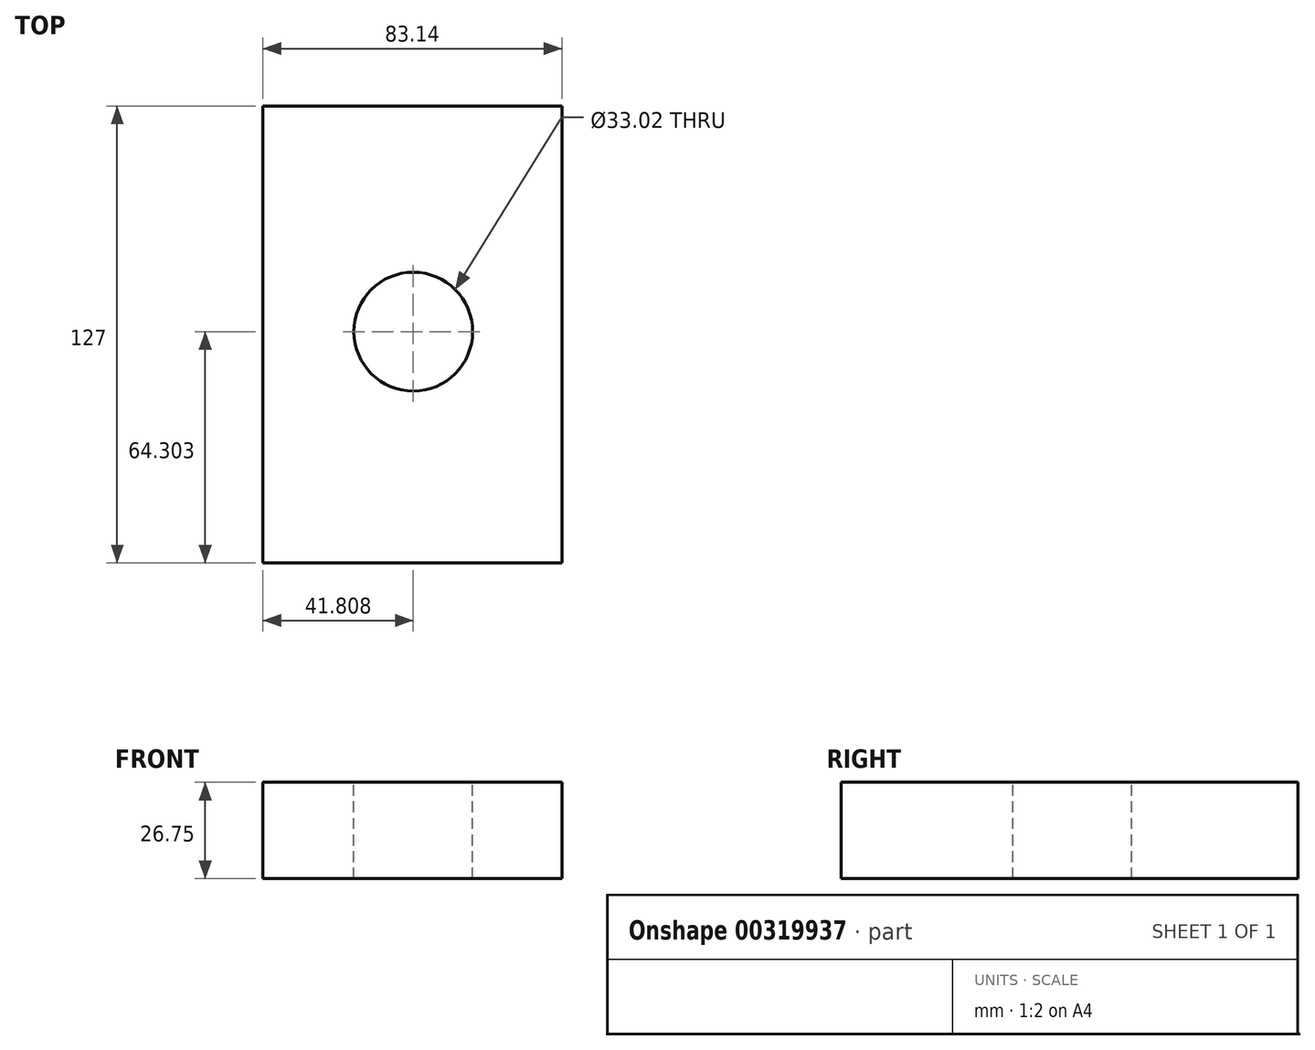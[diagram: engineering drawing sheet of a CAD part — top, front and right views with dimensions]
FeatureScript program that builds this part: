
annotation { "Feature Type Name" : "Feature", "Feature Type Description" : "" }
export const myFeature = defineFeature(function(context is Context, id is Id, definition is map)
    precondition{}
    {
        {
            var Q0;
            Q0=qCreatedBy(makeId("Front.planeOp"),FACE);
            var sketch = newSketch(context, id + "F0", { "sketchPlane" : qUnion([Q0])});
            skLineSegment(sketch, "E0", {"start": v(-54.46, 12.77) * mm, "end": v(-54.46, -13.98) * mm});
            skLineSegment(sketch, "E1", {"start": v(-54.46, -13.98) * mm, "end": v(28.68, -13.98) * mm});
            skLineSegment(sketch, "E2", {"start": v(28.68, -13.98) * mm, "end": v(28.68, 12.77) * mm});
            skLineSegment(sketch, "E3", {"start": v(-54.46, 12.77) * mm, "end": v(28.68, 12.77) * mm});
            skSolve(sketch);
        }
        {
            var Q0;
            Q0=makeQuery(id+"F0.imprint","IMPRINT",FACE,{"disambiguationData":[TD([[makeQuery(id+"F0.imprint","IMPRINT",EDGE,{"derivedFrom":sQuery(id+"F0.wireOp",EDGE,"E0")}),1.0]])]});
            extrude(context, id + "F1", {"entities" : qUnion([Q0]), "oppositeDirection" : true, "depth" : 127 * mm});
        }
        {
            var Q0;
            Q0=makeQuery(id+"F1.opExtrude","SWEPT_FACE",FACE,{"disambiguationData":[OSD([sQuery(id+"F0.wireOp",EDGE,"E3")])]});
            var sketch = newSketch(context, id + "F2", { "sketchPlane" : qUnion([Q0])});
            skCircle(sketch, "E4", {"center": v(-12.65, 64.3) * mm, "radius": 26.92 * mm});
            skSolve(sketch);
        }
        {
            var Q0;
            Q0=sQuery(id+"F2.wireOp",VERTEX,"E4.center");
            var Q1;
            Q1=makeQuery(id+"F1.opExtrude","SWEPT_BODY",BODY,{"disambiguationData":[OSD([sQuery(id+"F0.wireOp",EDGE,"E0"),sQuery(id+"F0.wireOp",EDGE,"E1"),sQuery(id+"F0.wireOp",EDGE,"E2"),sQuery(id+"F0.wireOp",EDGE,"E3")])]});
            hole(context, id + "F3", {"style" : HoleStyle.SIMPLE, "endStyle" : HoleEndStyle.THROUGH, "holeDiameter" : 33.02 * mm, "tappedDepth" : 12.7 * mm, "tapClearance" : 3, "locations" : qUnion([Q0]), "scope" : qUnion([Q1])});
        }
    });
